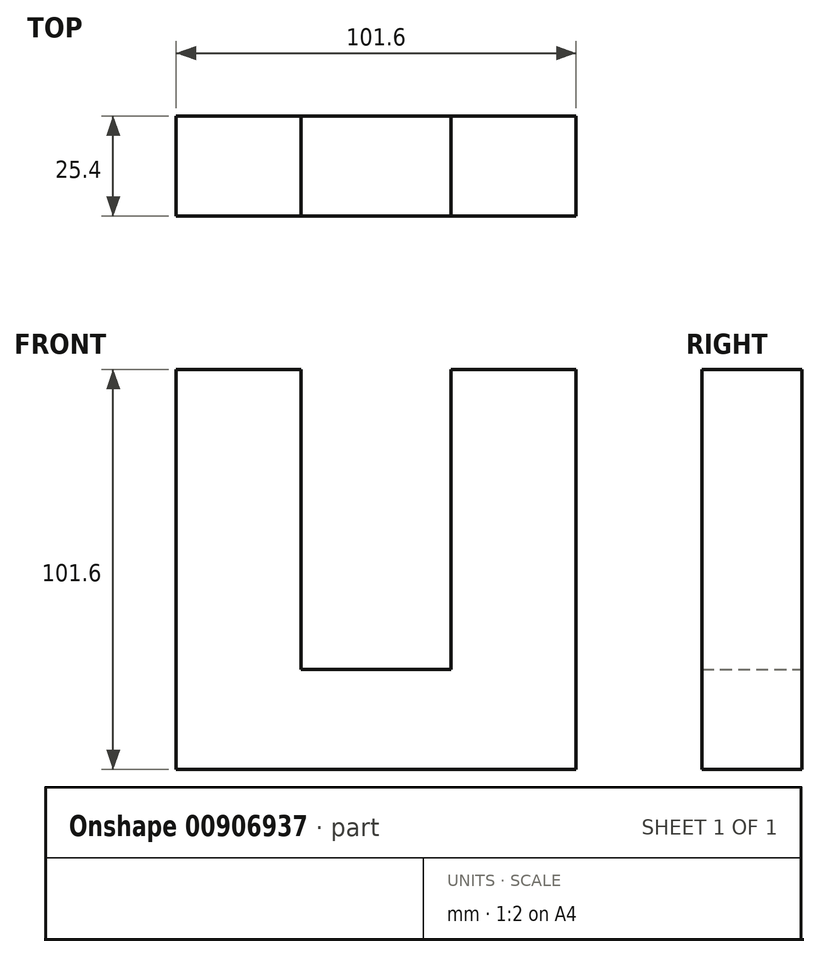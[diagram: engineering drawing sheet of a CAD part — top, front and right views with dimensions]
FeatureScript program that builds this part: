
annotation { "Feature Type Name" : "Feature", "Feature Type Description" : "" }
export const myFeature = defineFeature(function(context is Context, id is Id, definition is map)
    precondition{}
    {
        {
            var Q0;
            Q0=qCreatedBy(makeId("Front.planeOp"),FACE);
            var sketch = newSketch(context, id + "F0", { "sketchPlane" : qUnion([Q0])});
            skLineSegment(sketch, "E0.bottom", {"start": v(-50.8, -50.8) * mm, "end": v(50.8, -50.8) * mm});
            skLineSegment(sketch, "E0.top", {"start": v(-50.8, 50.8) * mm, "end": v(-19.05, 50.8) * mm});
            skLineSegment(sketch, "E0.left", {"start": v(-50.8, -50.8) * mm, "end": v(-50.8, 50.8) * mm});
            skLineSegment(sketch, "E0.right", {"start": v(50.8, -50.8) * mm, "end": v(50.8, 50.8) * mm});
            skPoint(sketch, "E0.middle", {"position": v(0, 0) * mm});
            skLineSegment(sketch, "E1", {"start": v(-19.05, 50.8) * mm, "end": v(-19.05, -25.4) * mm});
            skLineSegment(sketch, "E2", {"start": v(19.05, 50.8) * mm, "end": v(19.05, -25.4) * mm});
            skLineSegment(sketch, "E3.trimOffspring", {"start": v(19.05, 50.8) * mm, "end": v(50.8, 50.8) * mm});
            skLineSegment(sketch, "E4", {"start": v(-19.05, -25.4) * mm, "end": v(19.05, -25.4) * mm});
            skSolve(sketch);
        }
        {
            var Q0;
            Q0=makeQuery(id+"F0.imprint","IMPRINT",FACE,{"disambiguationData":[TD([[makeQuery(id+"F0.imprint","IMPRINT",EDGE,{"derivedFrom":sQuery(id+"F0.wireOp",EDGE,"E0.bottom")}),1.0]])]});
            extrude(context, id + "F1", {"entities" : qUnion([Q0]), "depth" : 25.4 * mm, "offsetDistance" : 25.4 * mm});
        }
    });
